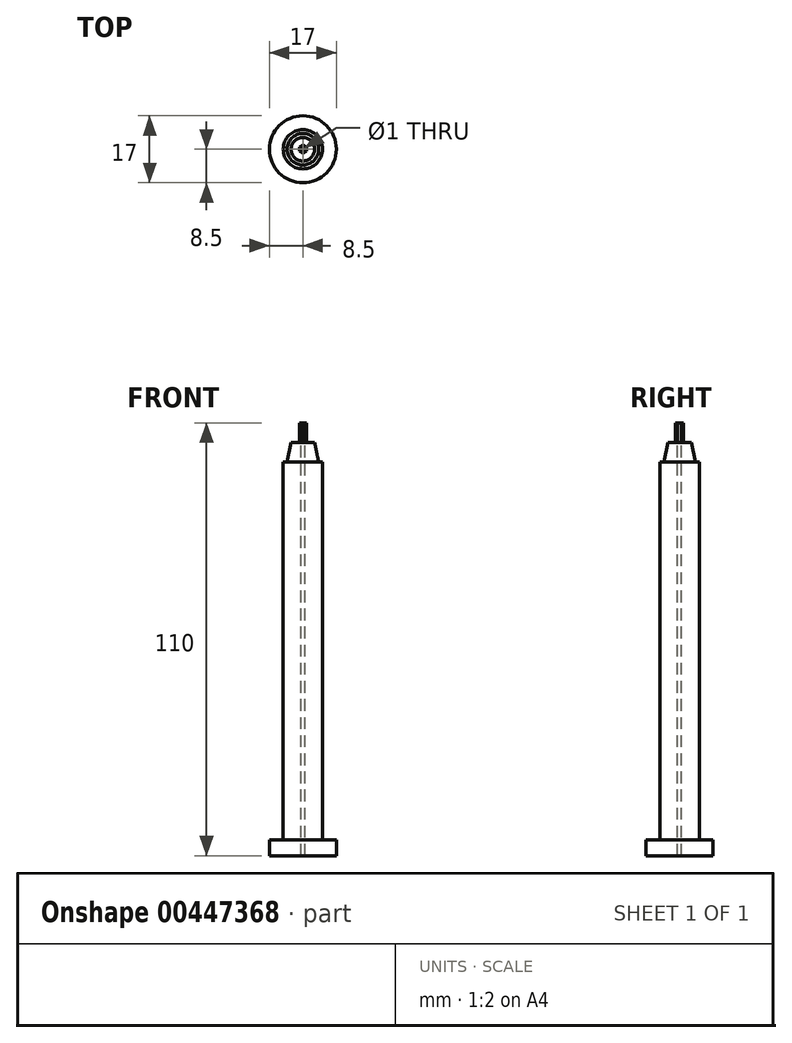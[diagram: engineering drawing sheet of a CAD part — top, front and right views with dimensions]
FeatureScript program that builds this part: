
annotation { "Feature Type Name" : "Feature", "Feature Type Description" : "" }
export const myFeature = defineFeature(function(context is Context, id is Id, definition is map)
    precondition{}
    {
        {
            var Q0;
            Q0=qCreatedBy(makeId("Top.planeOp"),FACE);
            var sketch = newSketch(context, id + "F0", { "sketchPlane" : qUnion([Q0])});
            skCircle(sketch, "E0", {"center": v(0, 0) * mm, "radius": 8.5 * mm});
            skSolve(sketch);
        }
        {
            var Q0;
            Q0=qSketchRegion(id+"F0",true);
            extrude(context, id + "F1", {"entities" : qUnion([Q0]), "depth" : 4 * mm});
        }
        {
            var Q0;
            Q0=qCreatedBy(makeId("Top.planeOp"),FACE);
            var sketch = newSketch(context, id + "F2", { "sketchPlane" : qUnion([Q0])});
            skCircle(sketch, "E1", {"center": v(0, 0) * mm, "radius": 5 * mm});
            skSolve(sketch);
        }
        {
            var Q0;
            Q0=qSketchRegion(id+"F2",true);
            extrude(context, id + "F3", {"entities" : qUnion([Q0]), "operationType" : NewBodyOperationType.ADD, "depth" : 100 * mm});
        }
        {
            var Q0;
            Q0=qCreatedBy(makeId("Right.planeOp"),FACE);
            var sketch = newSketch(context, id + "F4", { "sketchPlane" : qUnion([Q0])});
            skLineSegment(sketch, "E2", {"start": v(0, 105) * mm, "end": v(0, 100) * mm});
            skLineSegment(sketch, "E3", {"start": v(0, 100) * mm, "end": v(4, 100) * mm});
            skLineSegment(sketch, "E4", {"start": v(4, 100) * mm, "end": v(3, 105) * mm});
            skLineSegment(sketch, "E5", {"start": v(3, 105) * mm, "end": v(0, 105) * mm});
            skSolve(sketch);
        }
        {
            var Q0;
            Q0=makeQuery(id+"F4.imprint","IMPRINT",FACE,{"disambiguationData":[TD([[makeQuery(id+"F4.imprint","IMPRINT",EDGE,{"derivedFrom":sQuery(id+"F4.wireOp",EDGE,"E2")}),1.0]])]});
            var Q1;
            Q1=sQuery(id+"F4.wireOp",EDGE,"E2");
            revolve(context, id + "F5", {"operationType" : NewBodyOperationType.ADD, "entities" : qUnion([Q0]), "axis" : qUnion([Q1]), "revolveType" : RevolveType.FULL});
        }
        {
            var Q0;
            Q0=makeQuery(id+"F5.opRevolve","SWEPT_FACE",FACE,{"disambiguationData":[OSD([sQuery(id+"F4.wireOp",EDGE,"E5")])]});
            var sketch = newSketch(context, id + "F6", { "sketchPlane" : qUnion([Q0])});
            skCircle(sketch, "E6.cCircle", {"center": v(0, 0) * mm, "radius": 0.87 * mm, "construction": true});
            skLineSegment(sketch, "E6.0", {"start": v(0.87, 0.5) * mm, "end": v(0.87, -0.5) * mm});
            skLineSegment(sketch, "E6.1", {"start": v(0.87, -0.5) * mm, "end": v(0, -1) * mm});
            skLineSegment(sketch, "E6.2", {"start": v(0, -1) * mm, "end": v(-0.87, -0.5) * mm});
            skLineSegment(sketch, "E6.3", {"start": v(-0.87, -0.5) * mm, "end": v(-0.87, 0.5) * mm});
            skLineSegment(sketch, "E6.4", {"start": v(-0.87, 0.5) * mm, "end": v(0, 1) * mm});
            skLineSegment(sketch, "E6.5", {"start": v(0, 1) * mm, "end": v(0.87, 0.5) * mm});
            skPoint(sketch, "E6.0.midPoint", {"position": v(0.87, 0) * mm});
            skSolve(sketch);
        }
        {
            var Q0;
            Q0=makeQuery(id+"F6.imprint","IMPRINT",FACE,{"disambiguationData":[TD([[makeQuery(id+"F6.imprint","IMPRINT",EDGE,{"derivedFrom":sQuery(id+"F6.wireOp",EDGE,"E6.0")}),-1.0]])]});
            extrude(context, id + "F7", {"entities" : qUnion([Q0]), "operationType" : NewBodyOperationType.ADD, "depth" : 5 * mm});
        }
        {
            var Q0;
            Q0=makeQuery(id+"F7.opExtrude","CAP_FACE",FACE,{"disambiguationData":[OSD([sQuery(id+"F6.wireOp",EDGE,"E6.0"),sQuery(id+"F6.wireOp",EDGE,"E6.1"),sQuery(id+"F6.wireOp",EDGE,"E6.2"),sQuery(id+"F6.wireOp",EDGE,"E6.3"),sQuery(id+"F6.wireOp",EDGE,"E6.4"),sQuery(id+"F6.wireOp",EDGE,"E6.5")])],"isStart":false});
            var sketch = newSketch(context, id + "F8", { "sketchPlane" : qUnion([Q0])});
            skCircle(sketch, "E7", {"center": v(0, 0) * mm, "radius": 0.5 * mm});
            skSolve(sketch);
        }
        {
            var Q0;
            Q0 = qSketchRegion(id + "F8", true);
            extrude(context, id + "F9", {"entities" : qUnion([Q0]), "operationType" : NewBodyOperationType.REMOVE, "oppositeDirection" : true, "depth" : 120 * mm});
        }
    });
